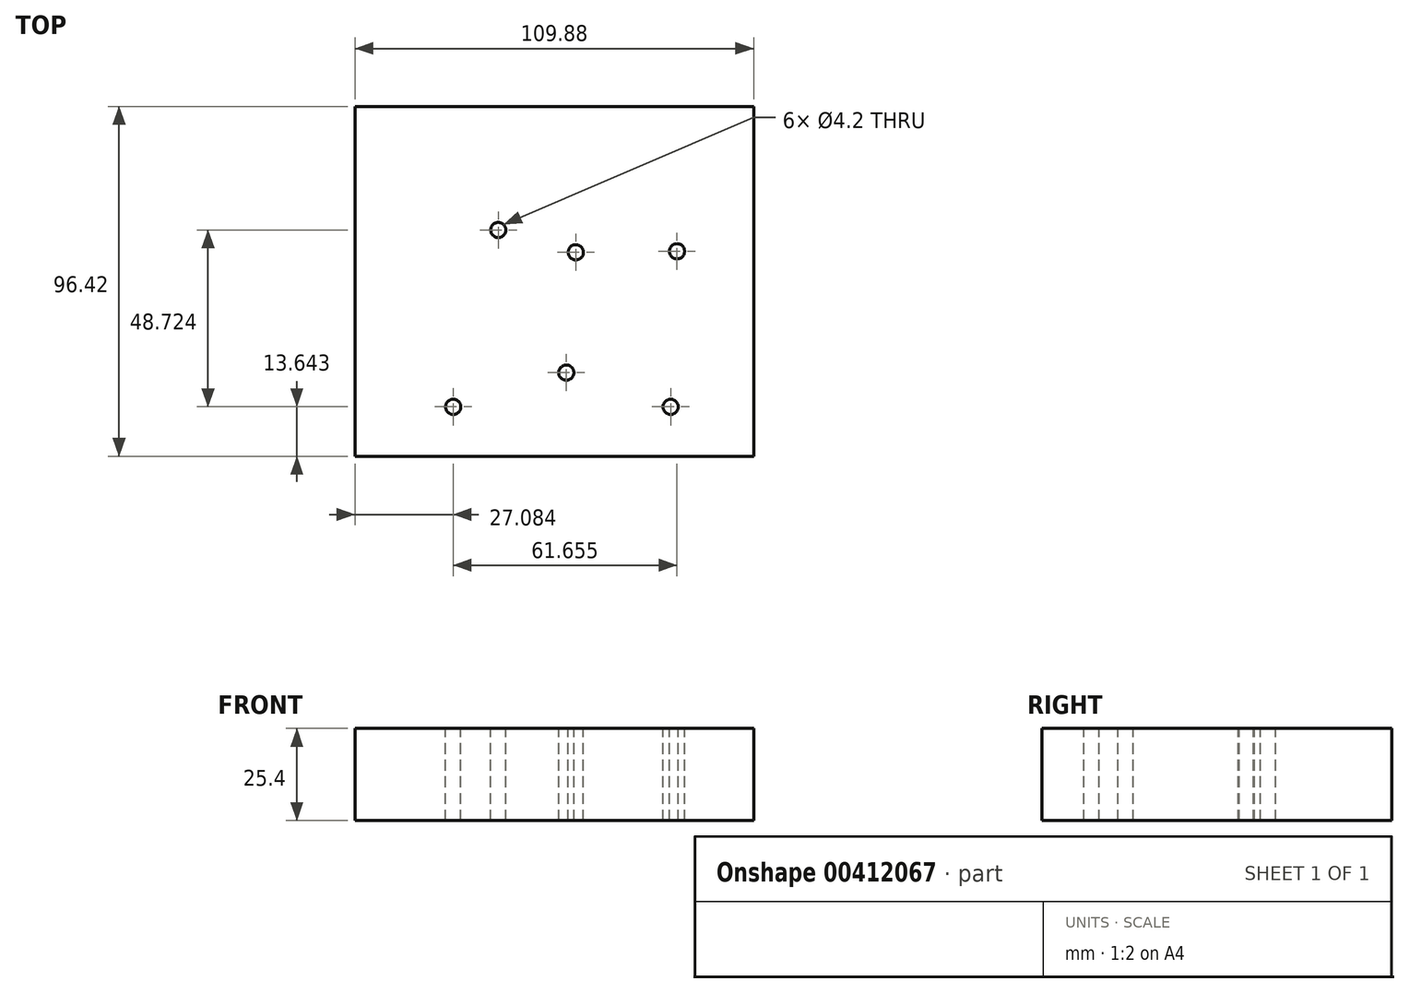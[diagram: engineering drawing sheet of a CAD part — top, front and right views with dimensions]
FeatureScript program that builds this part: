
annotation { "Feature Type Name" : "Feature", "Feature Type Description" : "" }
export const myFeature = defineFeature(function(context is Context, id is Id, definition is map)
    precondition{}
    {
        {
            var Q0;
            Q0=qCreatedBy(makeId("Top.planeOp"),FACE);
            var sketch = newSketch(context, id + "F0", { "sketchPlane" : qUnion([Q0])});
            skLineSegment(sketch, "E0.bottom", {"start": v(54.94, 48.2) * mm, "end": v(-54.94, 48.2) * mm});
            skLineSegment(sketch, "E0.top", {"start": v(54.94, -48.2) * mm, "end": v(-54.94, -48.2) * mm});
            skLineSegment(sketch, "E0.left", {"start": v(54.94, 48.2) * mm, "end": v(54.94, -48.2) * mm});
            skLineSegment(sketch, "E0.right", {"start": v(-54.94, 48.2) * mm, "end": v(-54.94, -48.2) * mm});
            skPoint(sketch, "E0.middle", {"position": v(0, 0) * mm});
            skSolve(sketch);
        }
        {
            var Q0;
            Q0 = qSketchRegion(id + "F0", true);
            extrude(context, id + "F1", {"entities" : qUnion([Q0]), "depth" : 25.4 * mm});
        }
        {
            var Q0;
            Q0=makeQuery(id+"F1.opExtrude","CAP_FACE",FACE,{"disambiguationData":[OSD([sQuery(id+"F0.wireOp",EDGE,"E0.bottom"),sQuery(id+"F0.wireOp",EDGE,"E0.top"),sQuery(id+"F0.wireOp",EDGE,"E0.left"),sQuery(id+"F0.wireOp",EDGE,"E0.right")])],"isStart":false});
            var sketch = newSketch(context, id + "F2", { "sketchPlane" : qUnion([Q0])});
            skPoint(sketch, "E1", {"position": v(-27.86, -34.57) * mm});
            skPoint(sketch, "E2", {"position": v(-15.43, 14.16) * mm});
            skPoint(sketch, "E3", {"position": v(33.8, 8.28) * mm});
            skPoint(sketch, "E4", {"position": v(32.06, -34.57) * mm});
            skPoint(sketch, "E5", {"position": v(3.3, -25.15) * mm});
            skPoint(sketch, "E6", {"position": v(5.92, 8.02) * mm});
            skSolve(sketch);
        }
        {
            var Q0;
            Q0=sQuery(id+"F2.wireOp",VERTEX,"E1");
            var Q1;
            Q1=sQuery(id+"F2.wireOp",VERTEX,"E2");
            var Q2;
            Q2=sQuery(id+"F2.wireOp",VERTEX,"E6");
            var Q3;
            Q3=sQuery(id+"F2.wireOp",VERTEX,"E3");
            var Q4;
            Q4=sQuery(id+"F2.wireOp",VERTEX,"E4");
            var Q5;
            Q5=sQuery(id+"F2.wireOp",VERTEX,"E5");
            var Q6;
            Q6=makeQuery(id+"F1.opExtrude","SWEPT_BODY",BODY,{"disambiguationData":[OSD([sQuery(id+"F0.wireOp",EDGE,"E0.bottom"),sQuery(id+"F0.wireOp",EDGE,"E0.top"),sQuery(id+"F0.wireOp",EDGE,"E0.left"),sQuery(id+"F0.wireOp",EDGE,"E0.right")])]});
            hole(context, id + "F3", {"style" : HoleStyle.SIMPLE, "endStyle" : HoleEndStyle.THROUGH, "standardTappedOrClearance" : lookupTablePath({ "standard" : "ISO", "engagement" : "75%", "pitch" : "0.8 mm", "size" : "M5", "type" : "Tapped" }), "standardBlindInLast" : lookupTablePath({ "standard" : "ISO", "engagement" : "75%", "pitch" : "0.8 mm", "size" : "M5", "type" : "Tapped" }), "holeDiameter" : 4.2 * mm, "showTappedDepth" : true, "isTappedThrough" : true, "tappedDepth" : 12 * mm, "tapClearance" : 3, "locations" : qUnion([Q0, Q1, Q2, Q3, Q4, Q5]), "scope" : qUnion([Q6]), "majorDiameter" : 5 * mm});
        }
    });
